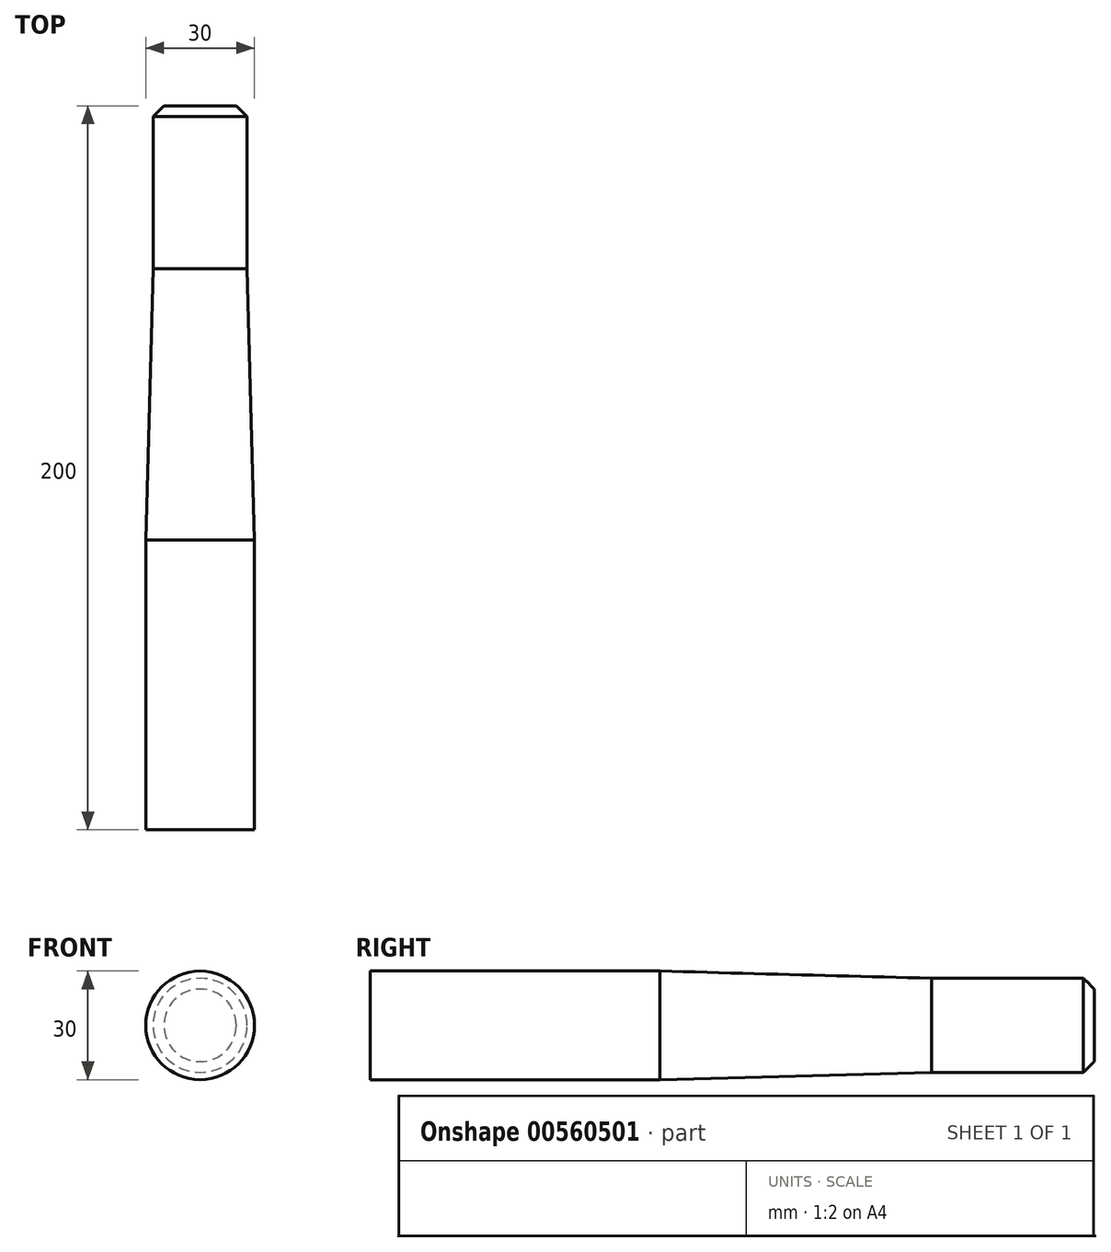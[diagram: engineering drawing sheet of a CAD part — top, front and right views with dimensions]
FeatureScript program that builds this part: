
annotation { "Feature Type Name" : "Feature", "Feature Type Description" : "" }
export const myFeature = defineFeature(function(context is Context, id is Id, definition is map)
    precondition{}
    {
        {
            var Q0;
            Q0=qCreatedBy(makeId("Front.planeOp"),FACE);
            var sketch = newSketch(context, id + "F0", { "sketchPlane" : qUnion([Q0])});
            skCircle(sketch, "E0", {"center": v(0, 0) * mm, "radius": 15 * mm});
            skSolve(sketch);
        }
        {
            var Q0;
            Q0=makeQuery(id+"F0.imprint","IMPRINT",FACE,{"disambiguationData":[TD([[makeQuery(id+"F0.imprint","IMPRINT",EDGE,{"derivedFrom":sQuery(id+"F0.wireOp",EDGE,"E0")}),1.0]])]});
            extrude(context, id + "F1", {"entities" : qUnion([Q0]), "depth" : 150 * mm, "offsetDistance" : 25 * mm});
        }
        {
            var Q0;
            Q0=makeQuery(id+"F1.opExtrude","CAP_FACE",FACE,{"disambiguationData":[OSD([sQuery(id+"F0.wireOp",EDGE,"E0")])],"isStart":true});
            var sketch = newSketch(context, id + "F2", { "sketchPlane" : qUnion([Q0])});
            skCircle(sketch, "E1", {"center": v(0, 0) * mm, "radius": 13 * mm});
            skCircle(sketch, "E2", {"center": v(0, 0) * mm, "radius": 15 * mm});
            skSolve(sketch);
        }
        {
            var Q0;
            Q0 = qSketchRegion(id + "F2", true);
            extrude(context, id + "F3", {"entities" : qUnion([Q0]), "operationType" : NewBodyOperationType.REMOVE, "oppositeDirection" : true, "depth" : 45 * mm, "offsetDistance" : 25 * mm});
        }
        {
            var Q0;
            Q0=qCreatedBy(makeId("Top.planeOp"),FACE);
            var sketch = newSketch(context, id + "F4", { "sketchPlane" : qUnion([Q0])});
            skLineSegment(sketch, "E3", {"start": v(13, -45) * mm, "end": v(15, -45) * mm});
            skLineSegment(sketch, "E4", {"start": v(15, -45) * mm, "end": v(15, -120) * mm});
            skLineSegment(sketch, "E5", {"start": v(15, -120) * mm, "end": v(13, -45) * mm});
            skLineSegment(sketch, "E6", {"start": v(10, 0) * mm, "end": v(13, 0) * mm});
            skLineSegment(sketch, "E7", {"start": v(13, 0) * mm, "end": v(13, -3) * mm});
            skLineSegment(sketch, "E8", {"start": v(13, -3) * mm, "end": v(10, 0) * mm});
            skSolve(sketch);
        }
        {
            var Q0;
            Q0 = qSketchRegion(id + "F4", true);
            var Q1;
            Q1=makeQuery(id+"F1.opExtrude","SWEPT_FACE",FACE,{"disambiguationData":[OSD([sQuery(id+"F0.wireOp",EDGE,"E0")])]});
            revolve(context, id + "F5", {"operationType" : NewBodyOperationType.REMOVE, "entities" : qUnion([Q0]), "axis" : qUnion([Q1]), "revolveType" : RevolveType.FULL, "oppositeDirection" : true});
        }
        {
            var Q0;
            Q0=makeQuery(id+"F1.opExtrude","CAP_FACE",FACE,{"disambiguationData":[OSD([sQuery(id+"F0.wireOp",EDGE,"E0")])],"isStart":false});
            var sketch = newSketch(context, id + "F6", { "sketchPlane" : qUnion([Q0])});
            skCircle(sketch, "E9", {"center": v(0, 0) * mm, "radius": 15 * mm});
            skSolve(sketch);
        }
        {
            var Q0;
            Q0 = qSketchRegion(id + "F6", true);
            extrude(context, id + "F7", {"entities" : qUnion([Q0]), "operationType" : NewBodyOperationType.ADD, "depth" : 50 * mm, "offsetDistance" : 25 * mm});
        }
    });
